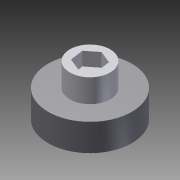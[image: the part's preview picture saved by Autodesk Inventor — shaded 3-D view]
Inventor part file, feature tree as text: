
AUTODESK INVENTOR PART (.ipt)
format: ipt  version: 2012 (Build 160160000, 160)  size: 814,592 bytes
history: native  units: mm
features: other x3, extrude x2, sketch x2, projected_geometry x1
ambient origin geometry x8: Origin, YZ Plane, XZ Plane, XY Plane, X Axis, Y Axis, Z Axis, Center Point
bodies: Solid1 (feature_tree)
feature tree (8):
  other  "MotorToGear.iam"
  other  "Spur Gear2:1"
  other  "MotorToGear.ipt:1"
  extrude  "Extrusion1"  Depth=10.0mm TaperAngle=0.0deg
  extrude  "Extrusion2"  [1 undecoded]
  sketch  "Sketch2"  dims[d0=10.0mm d1=10.0mm d2=0.0mm]
  sketch  "Sketch4"  dims[d3=10.0mm d4=0.0mm]
  projected_geometry  "Projected Loop1"
note: 1 required parameter value undecoded (feature->parameter linkage not recoverable at this tier; creation-order binding heuristic only, values carry confidence <= 0.55)
